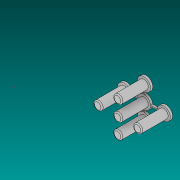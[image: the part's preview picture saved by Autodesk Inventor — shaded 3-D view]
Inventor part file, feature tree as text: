
AUTODESK INVENTOR PART (.ipt)
format: ipt  version: 2019 (Build 230136000, 136)  size: 680,960 bytes
history: native  units: mm
features: sketch x6, other x5, delete_face x5, extrude x4, fillet x3, boolean_combine x2
ambient origin geometry x8: Origin, YZ Plane, XZ Plane, XY Plane, X Axis, Y Axis, Z Axis, Center Point
bodies: Solid2 (feature_tree), Solid3 (feature_tree), Solid4 (feature_tree), Solid5 (feature_tree), Solid6 (feature_tree), Solid142 (feature_tree), Solid143 (feature_tree), Solid144 (feature_tree)
feature tree (25):
  other  "4301x60507x6_11:1"
  extrude  "Extrusion2"  Depth=4.0mm
  delete_face  "Delete Face2"
  delete_face  "Delete Face3"
  delete_face  "Delete Face4"
  delete_face  "Delete Face5"
  delete_face  "Delete Face6"
  extrude  "Extrusion3"  Depth=4.0mm
  fillet  "Fillet1"  Radius=4.0mm
  boolean_combine  "Combine1"
  extrude  "Extrusion4"  Depth=1.0mm
  sketch  "Sketch11"  dims[d22=1.0mm d23=1.0mm d32=1.0mm d33=0.0mm]
  boolean_combine  "Combine2"
  fillet  "Fillet2"  Radius=1.0mm
  sketch  "Sketch12"  dims[d34=4.0mm]
  extrude  "Extrusion5"  Depth=1.0mm
  fillet  "Fillet3"  Radius=1.0mm
  sketch  "Sketch8"  dims[d14=4.0mm d15=4.0mm]
  sketch  "Sketch9"  dims[d16=4.0mm d17=4.0mm d18=4.0mm]
  sketch  "Sketch10"  dims[d19=1.0mm d20=1.0mm d21=1.0mm]
  sketch  "Sketch13"  dims[d35=4.0mm d36=4.0mm d37=4.0mm d38=4.0mm d39=10.0mm d40=0.0mm d41=0.5mm d42=4.0mm d43=4.0mm d44=4.0mm d45=4.0mm d46=4.0mm d47=2.0mm d48=0.0mm d49=0.5mm d50=4.0mm d51=4.0mm d52=4.0mm d53=4.0mm d54=4.0mm d55=4.0mm d56=0.0mm d57=0.5mm]
  other  "4301x60507x6_3:1"
  other  "4301x60507x6_5:1"
  other  "4301x60507x6_7:1"
  other  "4301x60507x6_9:1"
